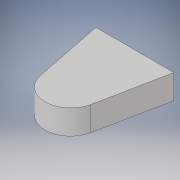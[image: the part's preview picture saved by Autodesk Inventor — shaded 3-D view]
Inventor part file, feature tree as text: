
AUTODESK INVENTOR PART (.ipt)
format: ipt  version: 2019 (Build 230136000, 136)  size: 95,232 bytes
history: native  units: mm
features: extrude x1, sketch x1
ambient origin geometry x8: Origin, YZ Plane, XZ Plane, XY Plane, X Axis, Y Axis, Z Axis, Center Point
bodies: Volumenkörper1 (feature_tree)
feature tree (2):
  extrude  "Extrusion1"  Depth=9.5mm
  sketch  "Skizze1"  dims[d0=20.0mm d1=32.0mm d2=39.0mm d3=35.0mm d4=9.5mm d5=0.0mm]
